# Revit family: ZETA_Коробка_Распределительная_100х100х40_IP40
name_source: partatom
category: Электрические приборы
units: mm (PartAtom-declared; Revit-internal decimal feet)

## family parameters
Всегда вертикально = Да
На основе рабочей плоскости = Да
Общий = Нет
При загрузке вырезать с полостями = Нет
Размер круглого соединителя = Использовать диаметр
Сохранять ориентацию аннотаций = Нет
Тип детали = Нормальный
Точка принадлежности помещению = Да

## types (1)
- 100х100х50_КР_IP_40
    ADSK_URL страницы изделия = https://nzeta.ru
    ADSK_Версия Revit = 2021
    ADSK_Версия семейства = v.1
    ADSK_Единица измерения = шт
    ADSK_Завод-изготовитель = АО «ЗЭТА»
    ADSK_КПД = 0
    ADSK_Классификация нагрузок = Прочее
    ADSK_Код изделия = zeta30320
    ADSK_Количество = 1
    ADSK_Количество фаз = 1
    ADSK_Количество фаз числовое = 1
    ADSK_Коэффициент мощности = 1
    ADSK_Кратность пускового тока = 0
    ADSK_Марка = КР 100х100х50
    ADSK_Масса = 0.324
    ADSK_Масса_Текст = 0.324
    ADSK_Материал наименование = Сталь оцинкованная
    ADSK_Наименование = Коробка распределительная стальная 100х100х50 IP40 ГОФРОМАТИК
    ADSK_Наименование краткое = Коробка 100х100х50
    ADSK_Напряжение = 0 В
    ADSK_Номинальная мощность = 0 Вт
    ADSK_Обозначение = КР
    ADSK_Полная мощность = 0 В·А
    ADSK_Пусковой ток = 0 А
    ADSK_Размер_Высота = 51 мм
    ADSK_Размер_Длина = 104 мм
    ADSK_Размер_Ширина = 104 мм
    ADSK_Степень защиты_IP = IP40
    ADSK_Ток = 0 А
    D1 = 21 мм
    D2 = 26 мм
    Hk = 7 мм
    LT = КР
    URL = https://nzeta.ru
    Видимость обозначения КР IP40 = Да
    Видимость отверстий = Нет
    Изготавливается по = ТУ 27.12.40-071-99856433-2024
    Изготовитель = АО «ЗЭТА»
    Климатическое исполнение = УХЛ 1.5
    Материал корпуса = Zeta_Сталь оцинкованная_цвет-серый
    Описание = Коробка распределительная стальная предназначена для обеспечения механической защиты, соединения, ответвления и протяжки электрических кабелей и проводов.
    Отметка по умолчанию = 1219 мм
    Температура эксплуатации = От -60°С до +150°С
    Тип_Геометрия = ZETA_Коробка_Распределительная_100х100х40(50) : 100х100х50_КР_IP_40
    Установочное отверстие для ввода = Без отверстий

## geometry (parser evidence)
native form markers: Sweep x1
no freeform markers — native parametric forms only
